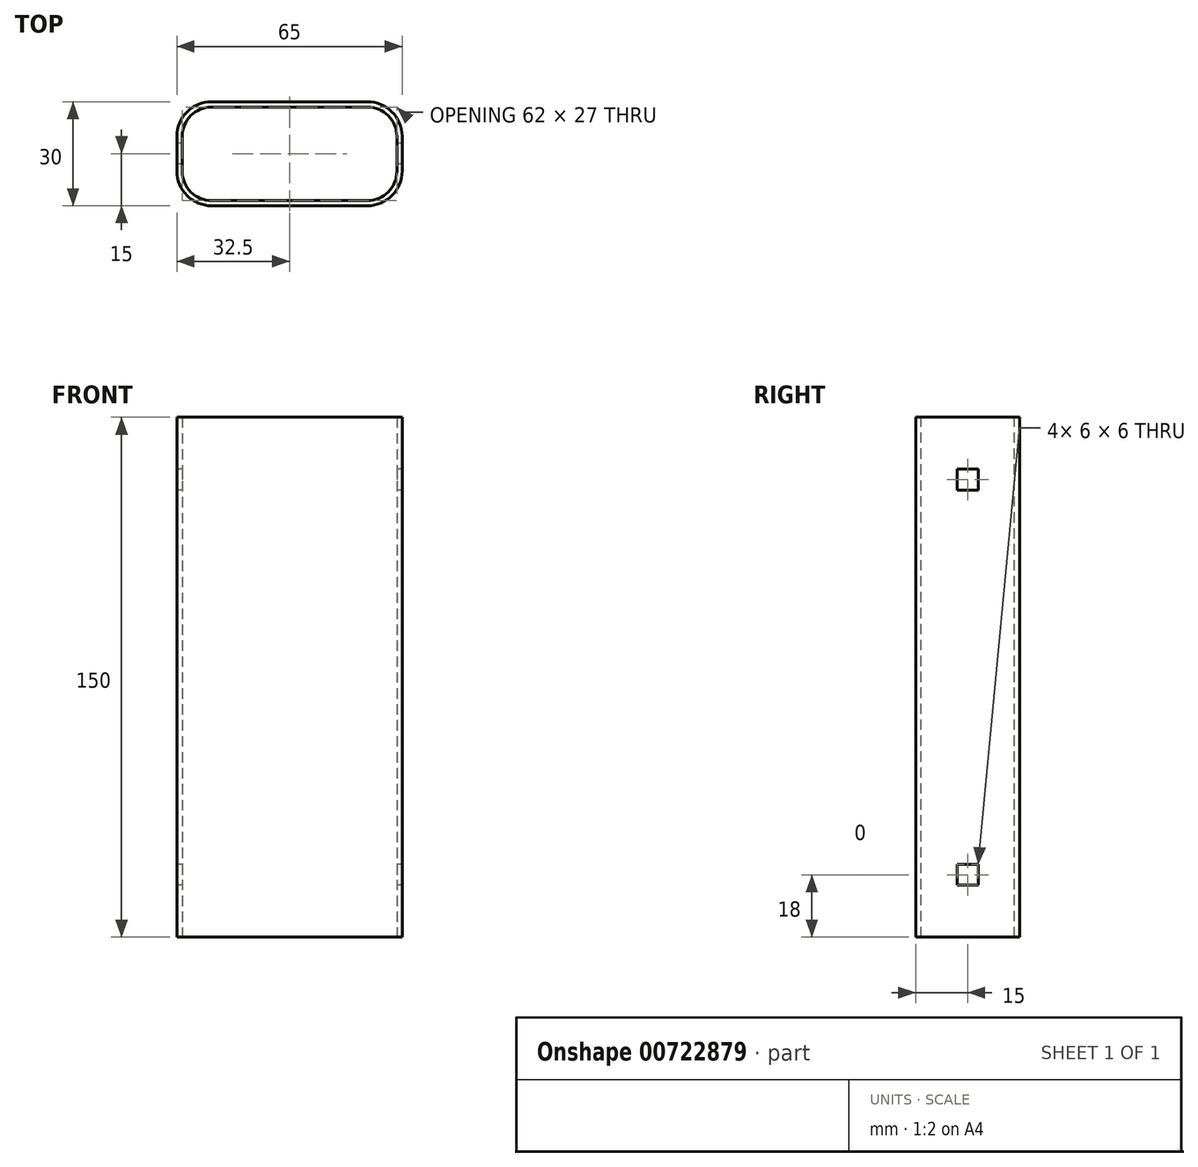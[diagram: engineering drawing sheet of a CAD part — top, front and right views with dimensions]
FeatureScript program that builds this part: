
annotation { "Feature Type Name" : "Feature", "Feature Type Description" : "" }
export const myFeature = defineFeature(function(context is Context, id is Id, definition is map)
    precondition{}
    {
        {
            var Q0;
            Q0=qCreatedBy(makeId("Top.planeOp"),FACE);
            var sketch = newSketch(context, id + "F0", { "sketchPlane" : qUnion([Q0])});
            skLineSegment(sketch, "E0.bottom", {"start": v(0, 0) * mm, "end": v(65, 0) * mm});
            skLineSegment(sketch, "E0.top", {"start": v(0, -30) * mm, "end": v(65, -30) * mm});
            skLineSegment(sketch, "E0.left", {"start": v(0, 0) * mm, "end": v(0, -30) * mm});
            skLineSegment(sketch, "E0.right", {"start": v(65, 0) * mm, "end": v(65, -30) * mm});
            skSolve(sketch);
        }
        {
            var Q0;
            Q0 = qSketchRegion(id + "F0", true);
            extrude(context, id + "F1", {"entities" : qUnion([Q0]), "depth" : 150 * mm, "offsetDistance" : 25 * mm});
        }
        {
            var Q0;
            Q0=makeQuery(id+"F1.opExtrude","SWEPT_EDGE",EDGE,{"disambiguationData":[OSD([sQuery(id+"F0.wireOp",EDGE,"E0.bottom"),sQuery(id+"F0.wireOp",EDGE,"E0.right")])]});
            var Q1;
            Q1=makeQuery(id+"F1.opExtrude","SWEPT_EDGE",EDGE,{"disambiguationData":[OSD([sQuery(id+"F0.wireOp",EDGE,"E0.top"),sQuery(id+"F0.wireOp",EDGE,"E0.right")])]});
            var Q2;
            Q2=makeQuery(id+"F1.opExtrude","SWEPT_EDGE",EDGE,{"disambiguationData":[OSD([sQuery(id+"F0.wireOp",EDGE,"E0.bottom"),sQuery(id+"F0.wireOp",EDGE,"E0.left")])]});
            var Q3;
            Q3=makeQuery(id+"F1.opExtrude","SWEPT_EDGE",EDGE,{"disambiguationData":[OSD([sQuery(id+"F0.wireOp",EDGE,"E0.top"),sQuery(id+"F0.wireOp",EDGE,"E0.left")])]});
            fillet(context, id + "F2", {"entities" : qUnion([Q0, Q1, Q2, Q3]), "radius" : 10 * mm, "tangentPropagation" : true, "allowEdgeOverflow" : false});
        }
        {
            var Q0;
            Q0=makeQuery(id+"F1.opExtrude","CAP_FACE",FACE,{"disambiguationData":[OSD([sQuery(id+"F0.wireOp",EDGE,"E0.bottom"),sQuery(id+"F0.wireOp",EDGE,"E0.top"),sQuery(id+"F0.wireOp",EDGE,"E0.left"),sQuery(id+"F0.wireOp",EDGE,"E0.right")])],"isStart":false});
            shell(context, id + "F3", {"entities" : qUnion([Q0]), "thickness" : 1.5 * mm});
        }
        {
            var Q0;
            Q0=makeQuery(id+"F3.opShell","OFFSET_FACE",FACE,{"disambiguationData":[OSD([sQuery(id+"F0.wireOp",EDGE,"E0.bottom"),sQuery(id+"F0.wireOp",EDGE,"E0.top"),sQuery(id+"F0.wireOp",EDGE,"E0.left"),sQuery(id+"F0.wireOp",EDGE,"E0.right")])]});
            extrude(context, id + "F4", {"entities" : qUnion([Q0]), "operationType" : NewBodyOperationType.REMOVE, "endBound" : BoundingType.UP_TO_NEXT, "oppositeDirection" : true, "depth" : 25 * mm, "offsetDistance" : 25 * mm});
        }
        {
            var Q0;
            Q0=makeQuery(id+"F1.opExtrude","SWEPT_FACE",FACE,{"disambiguationData":[OSD([sQuery(id+"F0.wireOp",EDGE,"E0.left")])]});
            var sketch = newSketch(context, id + "F5", { "sketchPlane" : qUnion([Q0])});
            skLineSegment(sketch, "E1.bottom", {"start": v(12, 15) * mm, "end": v(18, 15) * mm});
            skLineSegment(sketch, "E1.top", {"start": v(12, 21) * mm, "end": v(18, 21) * mm});
            skLineSegment(sketch, "E1.left", {"start": v(12, 15) * mm, "end": v(12, 21) * mm});
            skLineSegment(sketch, "E1.right", {"start": v(18, 15) * mm, "end": v(18, 21) * mm});
            skLineSegment(sketch, "E2.bottom", {"start": v(12, 129) * mm, "end": v(18, 129) * mm});
            skLineSegment(sketch, "E2.top", {"start": v(12, 135) * mm, "end": v(18, 135) * mm});
            skLineSegment(sketch, "E2.left", {"start": v(12, 129) * mm, "end": v(12, 135) * mm});
            skLineSegment(sketch, "E2.right", {"start": v(18, 129) * mm, "end": v(18, 135) * mm});
            skSolve(sketch);
        }
        {
            var Q0;
            Q0 = qSketchRegion(id + "F5", true);
            extrude(context, id + "F6", {"entities" : qUnion([Q0]), "operationType" : NewBodyOperationType.REMOVE, "endBound" : BoundingType.THROUGH_ALL, "oppositeDirection" : true, "depth" : 25 * mm, "offsetDistance" : 25 * mm});
        }
    });
